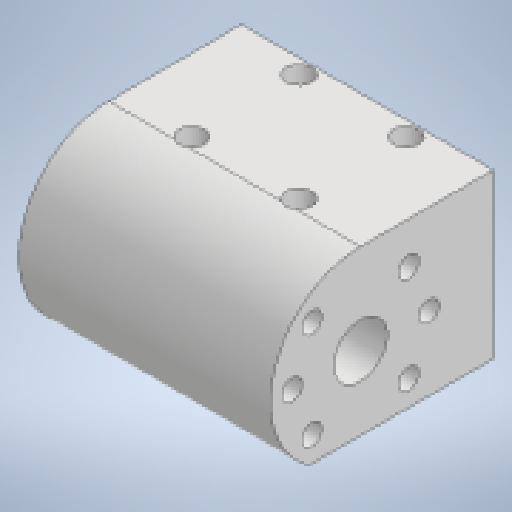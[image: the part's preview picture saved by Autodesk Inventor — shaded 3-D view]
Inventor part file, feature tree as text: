
AUTODESK INVENTOR PART (.ipt)
format: ipt  version: 2023 (Build 270158000, 158)  size: 240,128 bytes
history: native  units: mm
features: extrude x5, sketch x5, reference x4, other x3
ambient origin geometry x8: Origin, YZ Plane, XZ Plane, XY Plane, X Axis, Y Axis, Z Axis, Center Point
bodies: Solid1 (feature_tree)
feature tree (17):
  extrude  "Extrusion1"  Depth=3.0mm
  extrude  "Extrusion2"  Depth=32.0mm
  extrude  "Extrusion3"  Depth=2.0mm
  extrude  "Extrusion4"  Depth=32.0mm
  extrude  "Extrusion5"  Depth=15.0mm
  sketch  "Sketch1"  dims[d0=3.0mm d1=25.0mm]
  sketch  "Sketch2"  dims[d2=32.0mm d3=58.8mm]
  sketch  "Sketch3"  dims[d4=2.0mm d5=0.0mm d6=4.8mm]
  sketch  "Sketch4"  dims[d7=32.0mm d9=15.2mm]
  reference  "Reference1"
  reference  "Reference2"
  reference  "Reference3"
  reference  "Reference4"
  sketch  "Sketch5"  dims[d11=45.0deg d12=31.0mm d14=21.0mm d15=2.0mm d16=0.0mm d17=12.5mm d18=20.05mm d19=27.05mm d20=0.0mm d21=6.0mm d22=2.0mm d23=0.0mm d24=5.7mm d25=40.0mm d26=25.0mm d27=15.0mm d28=0.0mm]
  other  "<userpath>\Desktop\CNC_Project\Frame_Gantry_Carrier.iam"
  other  "Frame_Gantry_Carrier.iam"
  other  "MGN15H-Carrier:1"
